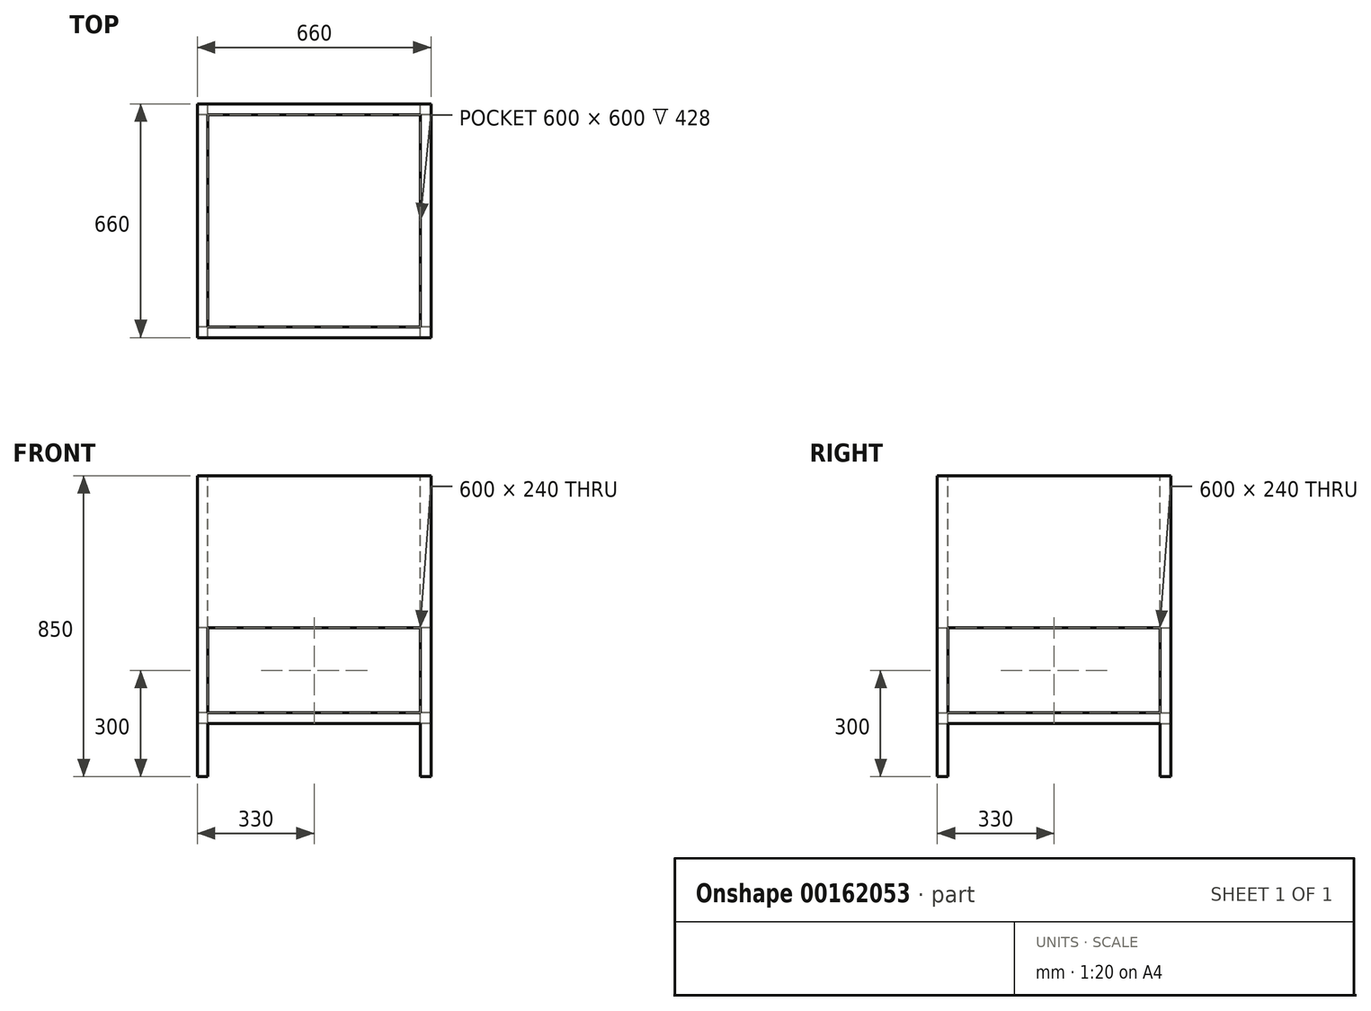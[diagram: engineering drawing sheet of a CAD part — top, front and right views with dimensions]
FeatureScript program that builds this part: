
annotation { "Feature Type Name" : "Feature", "Feature Type Description" : "" }
export const myFeature = defineFeature(function(context is Context, id is Id, definition is map)
    precondition{}
    {
        {
            var Q0;
            Q0=qCreatedBy(makeId("Right.planeOp"),FACE);
            var sketch = newSketch(context, id + "F0", { "sketchPlane" : qUnion([Q0])});
            skLineSegment(sketch, "E0", {"start": v(0, 0) * mm, "end": v(0, 450) * mm});
            skLineSegment(sketch, "E1", {"start": v(0, 450) * mm, "end": v(660, 450) * mm});
            skLineSegment(sketch, "E2", {"start": v(660, 450) * mm, "end": v(660, 0) * mm});
            skLineSegment(sketch, "E3", {"start": v(660, 0) * mm, "end": v(630, 0) * mm});
            skLineSegment(sketch, "E4", {"start": v(630, 0) * mm, "end": v(630, 150) * mm});
            skLineSegment(sketch, "E5", {"start": v(630, 150) * mm, "end": v(30, 150) * mm});
            skLineSegment(sketch, "E6", {"start": v(30, 150) * mm, "end": v(30, 0) * mm});
            skLineSegment(sketch, "E7", {"start": v(30, 0) * mm, "end": v(0, 0) * mm});
            skLineSegment(sketch, "E8.bottom", {"start": v(30, 420) * mm, "end": v(630, 420) * mm});
            skLineSegment(sketch, "E8.top", {"start": v(30, 180) * mm, "end": v(630, 180) * mm});
            skLineSegment(sketch, "E8.left", {"start": v(30, 420) * mm, "end": v(30, 180) * mm});
            skLineSegment(sketch, "E8.right", {"start": v(630, 420) * mm, "end": v(630, 180) * mm});
            skSolve(sketch);
        }
        {
            var Q0;
            Q0=qSketchRegion(id+"F0",true);
            extrude(context, id + "F1", {"entities" : qUnion([Q0]), "depth" : 660 * mm});
        }
        {
            var Q0;
            Q0=makeQuery(id+"F1.opExtrude","SWEPT_FACE",FACE,{"disambiguationData":[OSD([sQuery(id+"F0.wireOp",EDGE,"E1")])]});
            var sketch = newSketch(context, id + "F2", { "sketchPlane" : qUnion([Q0])});
            skLineSegment(sketch, "E9.bottom", {"start": v(630, 30) * mm, "end": v(30, 30) * mm});
            skLineSegment(sketch, "E9.top", {"start": v(630, 630) * mm, "end": v(30, 630) * mm});
            skLineSegment(sketch, "E9.left", {"start": v(630, 30) * mm, "end": v(630, 630) * mm});
            skLineSegment(sketch, "E9.right", {"start": v(30, 30) * mm, "end": v(30, 630) * mm});
            skLineSegment(sketch, "E10.top", {"start": v(0, 630) * mm, "end": v(385, 630) * mm});
            skSolve(sketch);
        }
        {
            var Q0;
            Q0=qSketchRegion(id+"F2",true);
            extrude(context, id + "F3", {"entities" : qUnion([Q0]), "operationType" : NewBodyOperationType.REMOVE, "endBound" : BoundingType.THROUGH_ALL, "oppositeDirection" : true, "depth" : 25 * mm});
        }
        {
            var Q0;
            Q0=makeQuery(id+"F1.opExtrude","SWEPT_FACE",FACE,{"disambiguationData":[OSD([sQuery(id+"F0.wireOp",EDGE,"E2")])]});
            var sketch = newSketch(context, id + "F4", { "sketchPlane" : qUnion([Q0])});
            skLineSegment(sketch, "E11.bottom", {"start": v(-630, 0) * mm, "end": v(-30, 0) * mm});
            skLineSegment(sketch, "E11.top", {"start": v(-630, 150) * mm, "end": v(-30, 150) * mm});
            skLineSegment(sketch, "E11.left", {"start": v(-630, 0) * mm, "end": v(-630, 150) * mm});
            skLineSegment(sketch, "E11.right", {"start": v(-30, 0) * mm, "end": v(-30, 150) * mm});
            skLineSegment(sketch, "E12.bottom", {"start": v(-630, 420) * mm, "end": v(-30, 420) * mm});
            skLineSegment(sketch, "E12.top", {"start": v(-630, 180) * mm, "end": v(-30, 180) * mm});
            skLineSegment(sketch, "E12.left", {"start": v(-630, 420) * mm, "end": v(-630, 180) * mm});
            skLineSegment(sketch, "E12.right", {"start": v(-30, 420) * mm, "end": v(-30, 180) * mm});
            skSolve(sketch);
        }
        {
            var Q0;
            Q0=qSketchRegion(id+"F4",true);
            extrude(context, id + "F5", {"entities" : qUnion([Q0]), "operationType" : NewBodyOperationType.REMOVE, "endBound" : BoundingType.THROUGH_ALL, "oppositeDirection" : true, "depth" : 25 * mm});
        }
        {
            var Q0;
            Q0=makeQuery(id+"F1.opExtrude","SWEPT_FACE",FACE,{"disambiguationData":[OSD([sQuery(id+"F0.wireOp",EDGE,"E1")])]});
            var sketch = newSketch(context, id + "F6", { "sketchPlane" : qUnion([Q0])});
            skLineSegment(sketch, "E13.bottom", {"start": v(660, 660) * mm, "end": v(0, 660) * mm});
            skLineSegment(sketch, "E13.top", {"start": v(660, 0) * mm, "end": v(0, 0) * mm});
            skLineSegment(sketch, "E13.left", {"start": v(660, 660) * mm, "end": v(660, 0) * mm});
            skLineSegment(sketch, "E13.right", {"start": v(0, 660) * mm, "end": v(0, 0) * mm});
            skLineSegment(sketch, "E14.bottom", {"start": v(630, 30) * mm, "end": v(30, 30) * mm});
            skLineSegment(sketch, "E14.top", {"start": v(630, 630) * mm, "end": v(30, 630) * mm});
            skLineSegment(sketch, "E14.left", {"start": v(630, 30) * mm, "end": v(630, 630) * mm});
            skLineSegment(sketch, "E14.right", {"start": v(30, 30) * mm, "end": v(30, 630) * mm});
            skSolve(sketch);
        }
        {
            var Q0;
            Q0=qSketchRegion(id+"F6",true);
            extrude(context, id + "F7", {"entities" : qUnion([Q0]), "operationType" : NewBodyOperationType.ADD, "depth" : 400 * mm});
        }
        {
            var Q0;
            Q0=makeQuery(id+"F5.boolean.opBoolean","COPY",FACE,{"disambiguationData":[TD([makeQuery(id+"F1.opExtrude","SWEPT_FACE",FACE,{"disambiguationData":[OSD([sQuery(id+"F0.wireOp",EDGE,"E2")])]})])],"derivedFrom":makeQuery(id+"F5.opExtrude","SWEPT_FACE",FACE,{"disambiguationData":[OSD([sQuery(id+"F4.wireOp",EDGE,"E12.bottom")])]})});
            var sketch = newSketch(context, id + "F8", { "sketchPlane" : qUnion([Q0])});
            skLineSegment(sketch, "E15.bottom", {"start": v(630, -660) * mm, "end": v(0, -660) * mm});
            skLineSegment(sketch, "E15.top", {"start": v(630, 0) * mm, "end": v(0, 0) * mm});
            skLineSegment(sketch, "E15.left", {"start": v(630, -660) * mm, "end": v(630, 0) * mm});
            skLineSegment(sketch, "E15.right", {"start": v(0, -660) * mm, "end": v(0, 0) * mm});
            skSolve(sketch);
        }
        {
            var Q0;
            Q0=qSketchRegion(id+"F8",true);
            extrude(context, id + "F9", {"entities" : qUnion([Q0]), "operationType" : NewBodyOperationType.ADD, "oppositeDirection" : true, "depth" : 2 * mm});
        }
    });
